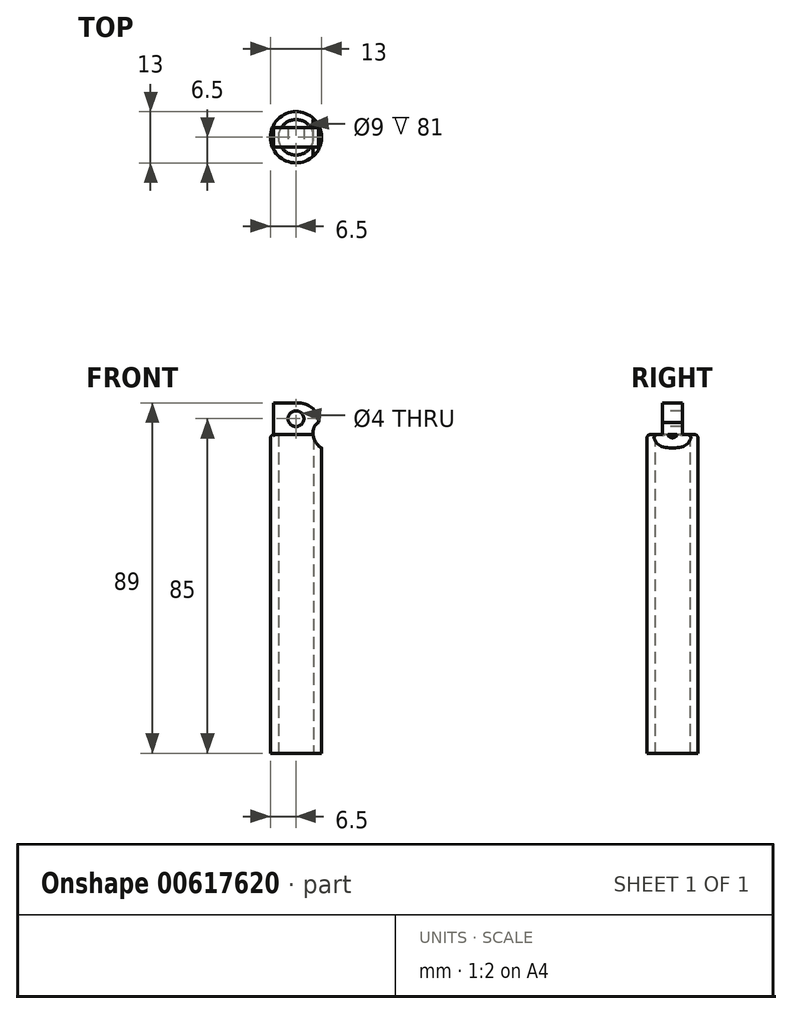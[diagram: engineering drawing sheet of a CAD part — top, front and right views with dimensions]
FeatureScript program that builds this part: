
annotation { "Feature Type Name" : "Feature", "Feature Type Description" : "" }
export const myFeature = defineFeature(function(context is Context, id is Id, definition is map)
    precondition{}
    {
        {
            var Q0;
            Q0=qCreatedBy(makeId("Top.planeOp"),FACE);
            var sketch = newSketch(context, id + "F0", { "sketchPlane" : qUnion([Q0])});
            skCircle(sketch, "E0", {"center": v(0, 0) * mm, "radius": 6.5 * mm});
            skSolve(sketch);
        }
        {
            var Q0;
            Q0=qSketchRegion(id+"F0",true);
            extrude(context, id + "F1", {"entities" : qUnion([Q0]), "depth" : 81 * mm, "offsetDistance" : 25 * mm});
        }
        {
            var Q0;
            Q0=makeQuery(id+"F1.opExtrude","CAP_FACE",FACE,{"disambiguationData":[OSD([sQuery(id+"F0.wireOp",EDGE,"E0")])],"isStart":false});
            var sketch = newSketch(context, id + "F2", { "sketchPlane" : qUnion([Q0])});
            skLineSegment(sketch, "E1.bottom", {"start": v(5.75, 2.5) * mm, "end": v(-5.75, 2.5) * mm});
            skLineSegment(sketch, "E1.top", {"start": v(5.75, -2.5) * mm, "end": v(-5.75, -2.5) * mm});
            skLineSegment(sketch, "E1.left", {"start": v(5.75, 2.5) * mm, "end": v(5.75, -2.5) * mm});
            skLineSegment(sketch, "E1.right", {"start": v(-5.75, 2.5) * mm, "end": v(-5.75, -2.5) * mm});
            skPoint(sketch, "E1.middle", {"position": v(0, 0) * mm});
            skSolve(sketch);
        }
        {
            var Q0;
            Q0=makeQuery(id+"F1.opExtrude","CAP_FACE",FACE,{"disambiguationData":[OSD([sQuery(id+"F0.wireOp",EDGE,"E0")])],"isStart":true});
            var Q1;
            Q1=makeQuery(id+"F1.opExtrude","CAP_FACE",FACE,{"disambiguationData":[OSD([sQuery(id+"F0.wireOp",EDGE,"E0")])],"isStart":false});
            shell(context, id + "F3", {"entities" : qUnion([Q0, Q1]), "thickness" : 2 * mm});
        }
        {
            var Q0;
            {var subQ1=makeQuery(id+"F1.opExtrude","CAP_EDGE",EDGE,{"disambiguationData":[OSD([sQuery(id+"F0.wireOp",EDGE,"E0")])],"isStart":false});var subQ10=sQuery(id+"F2.wireOp",EDGE,"E1.bottom");var subQ11=makeQuery(id+"F2.imprint","INTERSECT",VERTEX,{"disambiguationData":[OD(0.0)],"derivedFrom":[subQ1,subQ10]});Q0=makeQuery(id+"F2.imprint","IMPRINT",FACE,{"disambiguationData":[TD([[makeQuery(id+"F2.imprint","IMPRINT",EDGE,{"disambiguationData":[TD([[subQ11,-1.0]])],"derivedFrom":subQ10}),1.0]])]});}
            extrude(context, id + "F4", {"entities" : qUnion([Q0]), "operationType" : NewBodyOperationType.ADD, "depth" : 8 * mm, "offsetDistance" : 25 * mm});
        }
        {
            var Q0;
            Q0=makeQuery(id+"F4.opExtrude","SWEPT_FACE",FACE,{"disambiguationData":[OSD([sQuery(id+"F2.wireOp",EDGE,"E1.top")])]});
            var sketch = newSketch(context, id + "F5", { "sketchPlane" : qUnion([Q0])});
            skCircle(sketch, "E2", {"center": v(0, 85) * mm, "radius": 2 * mm});
            skPoint(sketch, "E2.centerSnap0", {"position": v(5.75, 85) * mm});
            skSolve(sketch);
        }
        {
            var Q0;
            Q0=qSketchRegion(id+"F5",true);
            extrude(context, id + "F6", {"entities" : qUnion([Q0]), "operationType" : NewBodyOperationType.REMOVE, "oppositeDirection" : true, "depth" : 5 * mm, "offsetDistance" : 25 * mm});
        }
        {
            var Q0;
            Q0=makeQuery(id+"F4.opExtrude","CAP_EDGE",EDGE,{"disambiguationData":[OSD([sQuery(id+"F2.wireOp",EDGE,"E1.left")])],"isStart":false});
            fillet(context, id + "F7", {"entities" : qUnion([Q0]), "radius" : 5 * mm, "tangentPropagation" : true, "allowEdgeOverflow" : false});
        }
        {
            var Q0;
            {var subQ1=sQuery(id+"F0.wireOp",EDGE,"E0");var subQ2=makeQuery(id+"F1.opExtrude","CAP_EDGE",EDGE,{"disambiguationData":[OSD([subQ1])],"isStart":false});var subQ3=sQuery(id+"F2.wireOp",EDGE,"E1.left");Q0=makeQuery(id+"F4.boolean.opBoolean","SPLIT",EDGE,{"disambiguationData":[TD([makeQuery(id+"F4.opExtrude","SWEPT_FACE",FACE,{"disambiguationData":[OSD([subQ3])]})])],"derivedFrom":subQ2});}
            var Q1;
            {var subQ1=sQuery(id+"F0.wireOp",EDGE,"E0");var subQ2=makeQuery(id+"F1.opExtrude","CAP_EDGE",EDGE,{"disambiguationData":[OSD([subQ1])],"isStart":false});var subQ4=sQuery(id+"F2.wireOp",EDGE,"E1.top");Q1=makeQuery(id+"F4.boolean.opBoolean","SPLIT",EDGE,{"disambiguationData":[TD([makeQuery(id+"F4.opExtrude","SWEPT_FACE",FACE,{"disambiguationData":[OSD([subQ4])]})])],"derivedFrom":subQ2});}
            var Q2;
            {var subQ0=sQuery(id+"F2.wireOp",EDGE,"E1.bottom");var subQ1=sQuery(id+"F0.wireOp",EDGE,"E0");var subQ2=makeQuery(id+"F1.opExtrude","CAP_EDGE",EDGE,{"disambiguationData":[OSD([subQ1])],"isStart":false});Q2=makeQuery(id+"F4.boolean.opBoolean","SPLIT",EDGE,{"disambiguationData":[TD([makeQuery(id+"F4.opExtrude","SWEPT_FACE",FACE,{"disambiguationData":[OSD([subQ0])]})])],"derivedFrom":subQ2});}
            fillet(context, id + "F8", {"entities" : qUnion([Q0, Q1, Q2]), "radius" : 1 * mm, "tangentPropagation" : true, "allowEdgeOverflow" : false});
        }
        {
            var Q0;
            Q0=makeQuery(id+"F4.opExtrude","SWEPT_FACE",FACE,{"disambiguationData":[OSD([sQuery(id+"F2.wireOp",EDGE,"E1.top")])]});
            var sketch = newSketch(context, id + "F9", { "sketchPlane" : qUnion([Q0])});
            skEllipse(sketch, "E3", {"center": v(6.95, 80.71) * mm, "majorRadius": 3.5 * mm, "minorRadius": 2.5 * mm, "majorAxis": v(-0.34, 0.94)});
            skSolve(sketch);
        }
        {
            var Q0;
            Q0=qSketchRegion(id+"F9",true);
            extrude(context, id + "F10", {"entities" : qUnion([Q0]), "operationType" : NewBodyOperationType.REMOVE, "depth" : 25 * mm, "offsetDistance" : 25 * mm, "hasSecondDirection" : true, "secondDirectionOppositeDirection" : true, "secondDirectionDepth" : 25 * mm});
        }
    });
